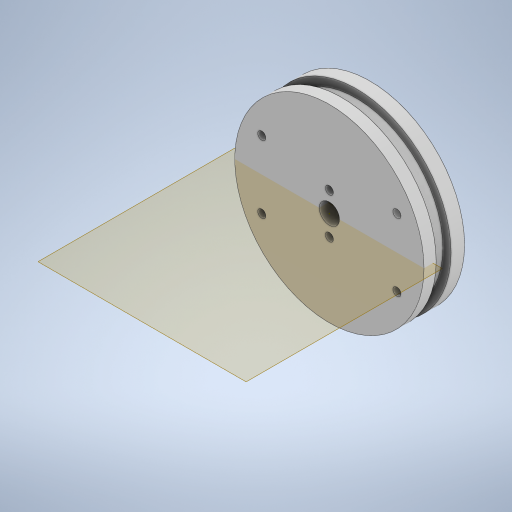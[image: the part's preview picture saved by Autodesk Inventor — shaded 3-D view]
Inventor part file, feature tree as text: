
AUTODESK INVENTOR PART (.ipt)
format: ipt  version: 2024 (Build 280153000, 153)  size: 658,944 bytes
history: native  units: mm
features: sketch x5, other x4, extrude x3, reference x2, plane x1, revolve x1
ambient origin geometry x8: Origin, YZ Plane, XZ Plane, XY Plane, X Axis, Y Axis, Z Axis, Center Point
bodies: Body1 (feature_tree)
feature tree (16):
  plane  "Work Plane1"
  revolve  "Revolution1"  [1 undecoded]
  sketch  "Sketch3"  dims[d5=11.0mm d6=6.0mm]
  extrude  "Extrusion2"  Depth=11.0mm
  extrude  "Extrusion3"  Depth=6.0mm
  extrude  "Extrusion4"  Depth=15.0mm
  sketch  "Sketch6"  dims[d12=11.0mm d13=0.0mm d14=5.5mm d15=0.0mm d16=0.0mm d17=5.0mm]
  sketch  "Sketch2"  dims[d3=30.0mm d4=10.0mm]
  reference  "Reference1"
  sketch  "Sketch4"  dims[d7=90.0deg d8=6.0mm]
  reference  "Reference2"
  sketch  "Sketch5"  dims[d9=10.0mm d10=0.0mm d11=15.0mm]
  other  "<userpath>\Documents\Inventor\robot arm\base_assembly.iam"
  other  "base_assembly.iam"
  other  "base:1"
  other  "Assembly1"
note: 1 required parameter value undecoded (feature->parameter linkage not recoverable at this tier; creation-order binding heuristic only, values carry confidence <= 0.55)
